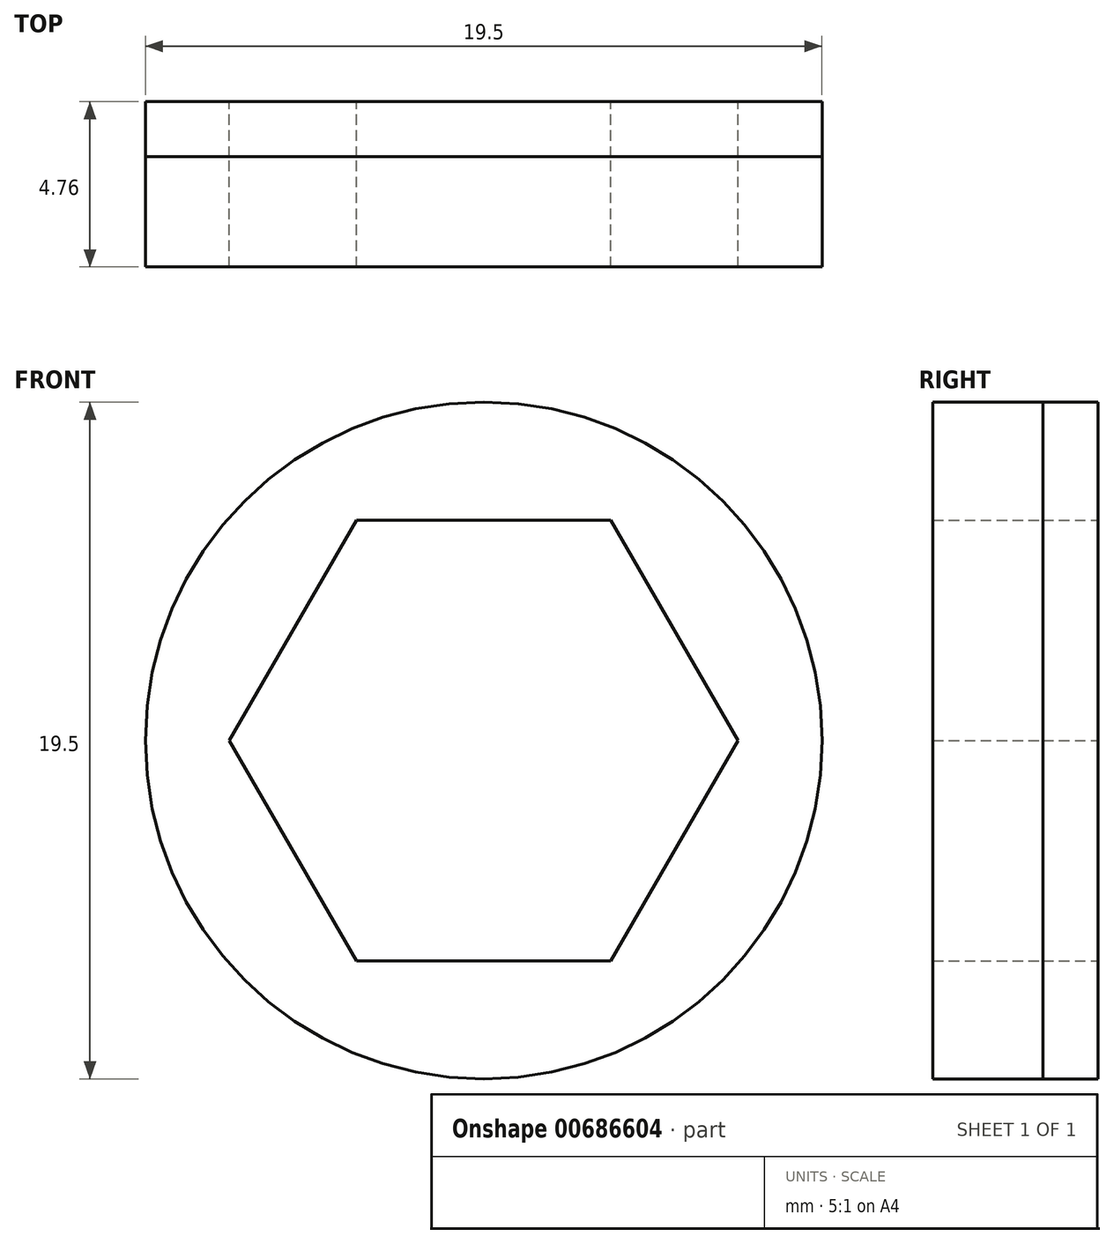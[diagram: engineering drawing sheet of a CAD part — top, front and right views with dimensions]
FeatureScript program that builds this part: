
annotation { "Feature Type Name" : "Feature", "Feature Type Description" : "" }
export const myFeature = defineFeature(function(context is Context, id is Id, definition is map)
    precondition{}
    {
        {
            var Q0;
            Q0=qCreatedBy(makeId("Front.planeOp"),FACE);
            var sketch = newSketch(context, id + "F0", { "sketchPlane" : qUnion([Q0])});
            skCircle(sketch, "E0", {"center": v(0, 0) * mm, "radius": 9.75 * mm});
            skCircle(sketch, "E1.cCircle", {"center": v(0, 0) * mm, "radius": 6.35 * mm, "construction": true});
            skLineSegment(sketch, "E1.0", {"start": v(-7.33, 0) * mm, "end": v(-3.67, 6.35) * mm});
            skLineSegment(sketch, "E1.1", {"start": v(-3.67, 6.35) * mm, "end": v(3.67, 6.35) * mm});
            skLineSegment(sketch, "E1.2", {"start": v(3.67, 6.35) * mm, "end": v(7.33, 0) * mm});
            skLineSegment(sketch, "E1.3", {"start": v(7.33, 0) * mm, "end": v(3.67, -6.35) * mm});
            skLineSegment(sketch, "E1.4", {"start": v(3.67, -6.35) * mm, "end": v(-3.67, -6.35) * mm});
            skLineSegment(sketch, "E1.5", {"start": v(-3.67, -6.35) * mm, "end": v(-7.33, 0) * mm});
            skPoint(sketch, "E1.0.midPoint", {"position": v(-5.5, 3.18) * mm});
            skSolve(sketch);
        }
        {
            var Q0;
            Q0 = qSketchRegion(id + "F0", true);
            extrude(context, id + "F1", {"entities" : qUnion([Q0]), "depth" : 1.59 * mm, "offsetDistance" : 25.4 * mm});
        }
        {
            var Q0;
            Q0=makeQuery(id+"F1.opExtrude","CAP_FACE",FACE,{"disambiguationData":[OSD([sQuery(id+"F0.wireOp",EDGE,"E0"),sQuery(id+"F0.wireOp",EDGE,"E1.0"),sQuery(id+"F0.wireOp",EDGE,"E1.1"),sQuery(id+"F0.wireOp",EDGE,"E1.2"),sQuery(id+"F0.wireOp",EDGE,"E1.3"),sQuery(id+"F0.wireOp",EDGE,"E1.4"),sQuery(id+"F0.wireOp",EDGE,"E1.5")])],"isStart":false});
            var sketch = newSketch(context, id + "F2", { "sketchPlane" : qUnion([Q0])});
            skLineSegment(sketch, "E2.0", {"start": v(-3.67, 6.35) * mm, "end": v(3.67, 6.35) * mm});
            skLineSegment(sketch, "E2.1", {"start": v(-7.33, 0) * mm, "end": v(-3.67, 6.35) * mm});
            skLineSegment(sketch, "E2.2", {"start": v(-3.67, -6.35) * mm, "end": v(-7.33, 0) * mm});
            skLineSegment(sketch, "E2.3", {"start": v(3.67, -6.35) * mm, "end": v(-3.67, -6.35) * mm});
            skLineSegment(sketch, "E2.4", {"start": v(7.33, 0) * mm, "end": v(3.67, -6.35) * mm});
            skLineSegment(sketch, "E2.5", {"start": v(3.67, 6.35) * mm, "end": v(7.33, 0) * mm});
            skCircle(sketch, "E2.6", {"center": v(0, 0) * mm, "radius": 9.75 * mm});
            skPoint(sketch, "E2.7", {"position": v(-5.5, -3.17) * mm});
            skSolve(sketch);
        }
        {
            var Q0;
            Q0 = qSketchRegion(id + "F2", true);
            extrude(context, id + "F3", {"entities" : qUnion([Q0]), "depth" : 3.17 * mm, "offsetDistance" : 25.4 * mm});
        }
    });
